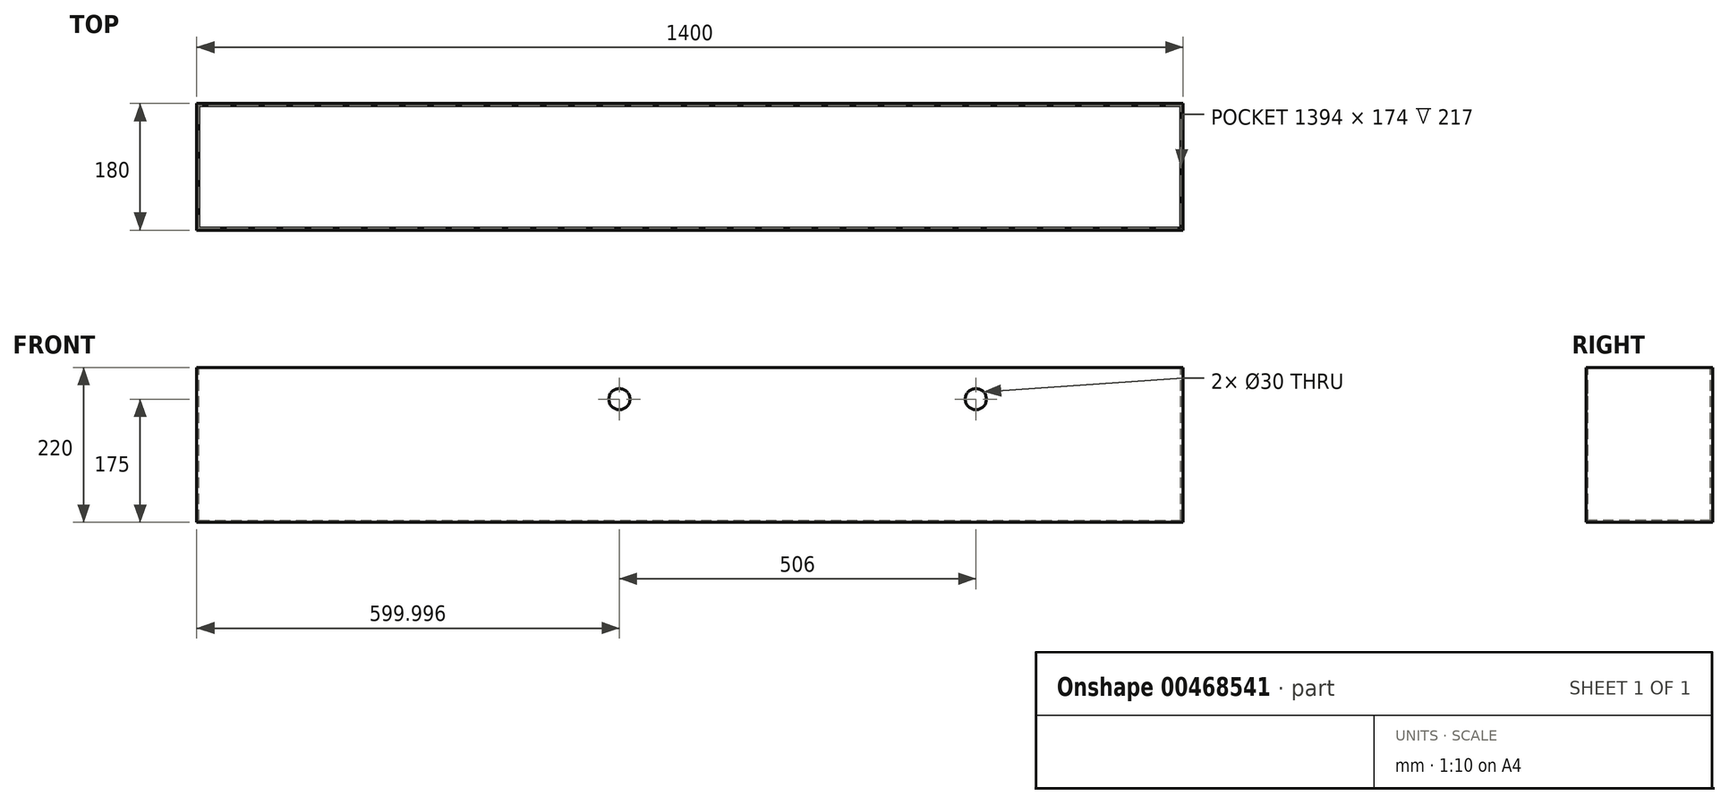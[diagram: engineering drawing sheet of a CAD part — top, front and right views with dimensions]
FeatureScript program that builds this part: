
annotation { "Feature Type Name" : "Feature", "Feature Type Description" : "" }
export const myFeature = defineFeature(function(context is Context, id is Id, definition is map)
    precondition{}
    {
        {
            var Q0;
            Q0=qCreatedBy(makeId("Top.planeOp"),FACE);
            var sketch = newSketch(context, id + "F0", { "sketchPlane" : qUnion([Q0])});
            skLineSegment(sketch, "E0.bottom", {"start": v(-46.21, 143.95) * mm, "end": v(1353.79, 143.95) * mm});
            skLineSegment(sketch, "E0.top", {"start": v(-46.21, -36.05) * mm, "end": v(1353.79, -36.05) * mm});
            skLineSegment(sketch, "E0.left", {"start": v(-46.21, 143.95) * mm, "end": v(-46.21, -36.05) * mm});
            skLineSegment(sketch, "E0.right", {"start": v(1353.79, 143.95) * mm, "end": v(1353.79, -36.05) * mm});
            skSolve(sketch);
        }
        {
            var Q0;
            Q0=makeQuery(id+"F0.imprint","IMPRINT",FACE,{"disambiguationData":[TD([[makeQuery(id+"F0.imprint","IMPRINT",EDGE,{"derivedFrom":sQuery(id+"F0.wireOp",EDGE,"E0.bottom")}),-1.0]])]});
            extrude(context, id + "F1", {"entities" : qUnion([Q0]), "depth" : 220 * mm, "offsetDistance" : 25 * mm});
        }
        {
            var Q0;
            Q0=makeQuery(id+"F1.opExtrude","CAP_FACE",FACE,{"disambiguationData":[OSD([sQuery(id+"F0.wireOp",EDGE,"E0.bottom"),sQuery(id+"F0.wireOp",EDGE,"E0.top"),sQuery(id+"F0.wireOp",EDGE,"E0.left"),sQuery(id+"F0.wireOp",EDGE,"E0.right")])],"isStart":false});
            var sketch = newSketch(context, id + "F2", { "sketchPlane" : qUnion([Q0])});
            skLineSegment(sketch, "E1.bottom", {"start": v(-43.21, 140.95) * mm, "end": v(1350.79, 140.95) * mm});
            skLineSegment(sketch, "E1.top", {"start": v(-43.21, -33.05) * mm, "end": v(1350.79, -33.05) * mm});
            skLineSegment(sketch, "E1.left", {"start": v(-43.21, 140.95) * mm, "end": v(-43.21, -33.05) * mm});
            skLineSegment(sketch, "E1.right", {"start": v(1350.79, 140.95) * mm, "end": v(1350.79, -33.05) * mm});
            skSolve(sketch);
        }
        {
            var Q0;
            Q0 = qSketchRegion(id + "F2", true);
            extrude(context, id + "F3", {"entities" : qUnion([Q0]), "operationType" : NewBodyOperationType.REMOVE, "oppositeDirection" : true, "depth" : 217 * mm, "offsetDistance" : 25 * mm});
        }
        {
            var Q0;
            Q0=makeQuery(id+"F1.opExtrude","SWEPT_FACE",FACE,{"disambiguationData":[OSD([sQuery(id+"F0.wireOp",EDGE,"E0.top")])]});
            var sketch = newSketch(context, id + "F4", { "sketchPlane" : qUnion([Q0])});
            skLineSegment(sketch, "E2", {"start": v(1353.79, 175) * mm, "end": v(-46.21, 175) * mm, "construction": true});
            skCircle(sketch, "E3", {"center": v(553.79, 175) * mm, "radius": 15 * mm});
            skCircle(sketch, "E4", {"center": v(1059.79, 175) * mm, "radius": 15 * mm});
            skSolve(sketch);
        }
        {
            var Q0;
            Q0=makeQuery(id+"F4.imprint","IMPRINT",FACE,{"disambiguationData":[TD([[makeQuery(id+"F4.imprint","IMPRINT",EDGE,{"derivedFrom":sQuery(id+"F4.wireOp",EDGE,"E3")}),1.0]])]});
            var Q1;
            Q1=makeQuery(id+"F4.imprint","IMPRINT",FACE,{"disambiguationData":[TD([[makeQuery(id+"F4.imprint","IMPRINT",EDGE,{"derivedFrom":sQuery(id+"F4.wireOp",EDGE,"E4")}),1.0]])]});
            extrude(context, id + "F5", {"entities" : qUnion([Q0, Q1]), "operationType" : NewBodyOperationType.REMOVE, "endBound" : BoundingType.UP_TO_NEXT, "oppositeDirection" : true, "depth" : 25 * mm, "offsetDistance" : 25 * mm});
        }
    });
